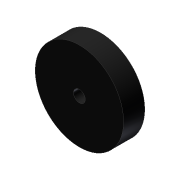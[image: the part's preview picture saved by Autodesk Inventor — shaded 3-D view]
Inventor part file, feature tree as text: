
AUTODESK INVENTOR PART (.ipt)
format: ipt  version: 2012 (Build 160160000, 160)  size: 72,704 bytes
history: native  units: in
note: dims shown in document units (in); Inventor stores cm internally (conversion verified against a paired STEP export)
features: extrude x1, sketch x1
ambient origin geometry x8: Origin, YZ Plane, XZ Plane, XY Plane, X Axis, Y Axis, Z Axis, Center Point
bodies: Solid1 (feature_tree)
feature tree (2):
  extrude  "Extrusion1"  Depth=1.0in
  sketch  "Sketch1"  dims[d0=7.5in d1=1.0in d2=1.8in d3=0.0in]
